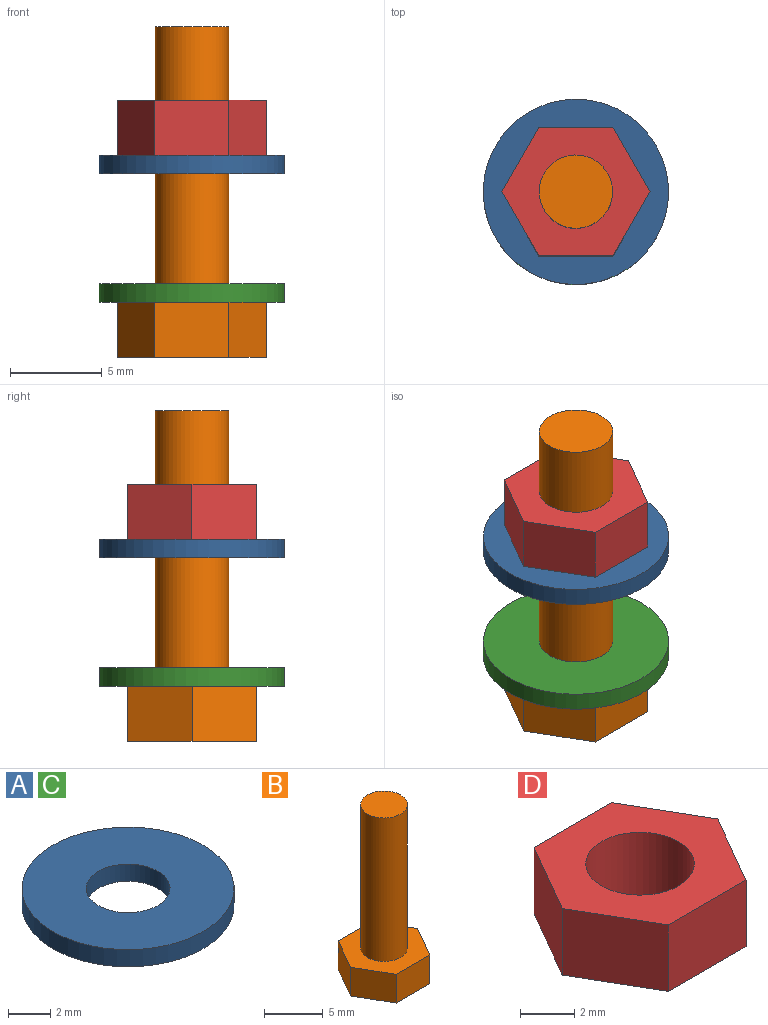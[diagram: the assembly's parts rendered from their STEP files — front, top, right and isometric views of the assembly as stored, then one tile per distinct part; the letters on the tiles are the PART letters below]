
ASSEMBLY  parts=4 mates=3
PART A: 4 faces, bbox 10.1x10.1x1 mm
  f0: cylinder r=2mm len=4mm, axis (0,0,-1), area 12.6mm2, adj f2,f3
  f1: cylinder r=5.05mm len=10.1mm, axis (0,0,-1), area 31.7mm2, adj f2,f3
  f2: plane 10.1x10.1mm, normal (0,0,1), area 67.6mm2, adj f0,f1
  f3: plane 10.1x10.1mm, normal (0,0,-1), area 67.6mm2, adj f0,f1
PART B: 10 faces, bbox 8.1x7x18 mm
  f0: plane 4.04x3mm, normal (0,1,0), area 12.1mm2, adj f1,f5,f6,f7
  f1: plane 3.5x3mm, normal (-0.87,0.5,0), area 12.1mm2, adj f0,f2,f6,f7
  f2: plane 3.5x3mm, normal (-0.87,-0.5,0), area 12.1mm2, adj f1,f3,f6,f7
  f3: plane 4.04x3mm, normal (0,-1,0), area 12.1mm2, adj f2,f4,f6,f7
  f4: plane 3.5x3mm, normal (0.87,-0.5,0), area 12.1mm2, adj f3,f5,f6,f7
  f5: plane 3.5x3mm, normal (0.87,0.5,0), area 12.1mm2, adj f0,f4,f6,f7
  f6: plane 8.08x7mm, normal (0,0,-1), area 42.4mm2, adj f0,f1,f2,f3,f4,f5
  f7: plane 8.08x7mm, normal (0,0,1), area 29.9mm2, adj f0,f1,f2,f3,f4,f5,f8
  f8: cylinder r=2mm len=15mm, axis (0,0,-1), area 188.5mm2, adj f7,f9
  f9: plane 4x4mm, normal (0,0,1), area 12.6mm2, adj f8
PART C: same geometry as A
PART D: 9 faces, bbox 8.1x7x3 mm
  f0: plane 4.04x3mm, normal (0,-1,0), area 12.1mm2, adj f1,f5,f7,f8
  f1: plane 3.5x3mm, normal (0.87,-0.5,0), area 12.1mm2, adj f0,f2,f7,f8
  f2: plane 3.5x3mm, normal (0.87,0.5,0), area 12.1mm2, adj f1,f3,f7,f8
  f3: plane 4.04x3mm, normal (0,1,0), area 12.1mm2, adj f2,f4,f7,f8
  f4: plane 3.5x3mm, normal (-0.87,0.5,0), area 12.1mm2, adj f3,f5,f7,f8
  f5: plane 3.5x3mm, normal (-0.87,-0.5,0), area 12.1mm2, adj f0,f4,f7,f8
  f6: cylinder r=2mm len=4mm, axis (0,0,-1), area 37.7mm2, adj f7,f8
  f7: plane 8.08x7mm, normal (0,0,1), area 29.9mm2, adj f0,f1,f2,f3,f4,f5,f6
  f8: plane 8.08x7mm, normal (0,0,-1), area 29.9mm2, adj f0,f1,f2,f3,f4,f5,f6
PLACE A t=(180,22.92,3)mm
PLACE B t=(180,-19.08,-4)mm
PLACE C t=(180,22.92,-4)mm
PLACE D rot(axis=(1,0,0),180deg) t=(180,-40.08,7)mm
MATE fastened A.f0 <-> C.f0  axis (0,0,-1) through (180,-19.08,3)mm
MATE fastened D.f6 <-> A.f0  axis (0,0,1) through (180,-19.08,4)mm
MATE fastened C.f0 <-> B.f8  axis (0,0,-1) through (180,-19.08,-4)mm
